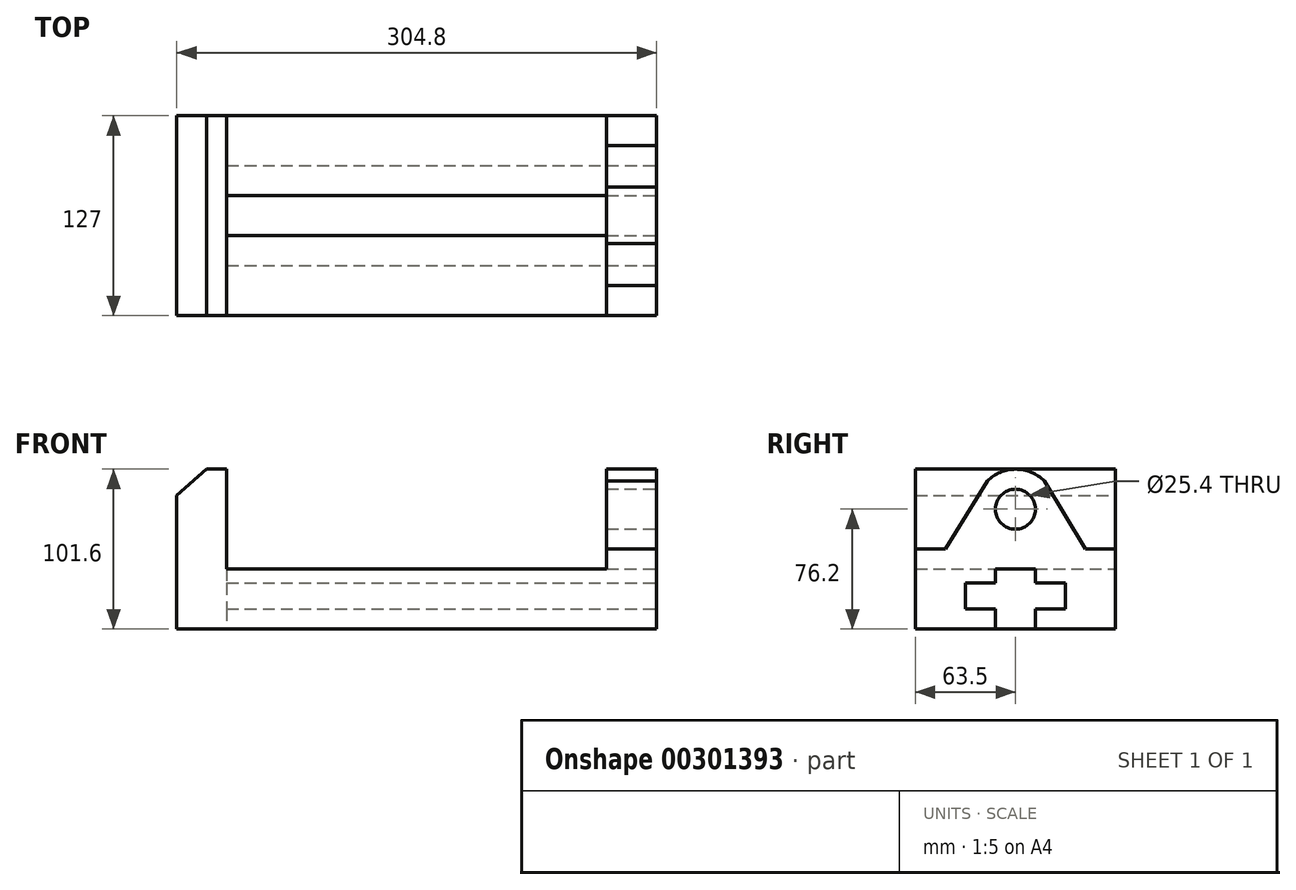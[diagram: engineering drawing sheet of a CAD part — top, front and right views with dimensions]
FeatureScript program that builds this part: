
annotation { "Feature Type Name" : "Feature", "Feature Type Description" : "" }
export const myFeature = defineFeature(function(context is Context, id is Id, definition is map)
    precondition{}
    {
        {
            var Q0;
            Q0=qCreatedBy(makeId("Front.planeOp"),FACE);
            var sketch = newSketch(context, id + "F0", { "sketchPlane" : qUnion([Q0])});
            skLineSegment(sketch, "E0", {"start": v(0, 0) * mm, "end": v(304.8, 0) * mm});
            skLineSegment(sketch, "E1", {"start": v(304.8, 0) * mm, "end": v(304.8, 101.6) * mm});
            skLineSegment(sketch, "E2", {"start": v(304.8, 101.6) * mm, "end": v(273.05, 101.6) * mm});
            skLineSegment(sketch, "E3", {"start": v(273.05, 101.6) * mm, "end": v(273.05, 38.1) * mm});
            skLineSegment(sketch, "E4", {"start": v(273.05, 38.1) * mm, "end": v(31.75, 38.1) * mm});
            skLineSegment(sketch, "E5", {"start": v(31.75, 38.1) * mm, "end": v(31.75, 101.6) * mm});
            skLineSegment(sketch, "E6", {"start": v(31.75, 101.6) * mm, "end": v(19.05, 101.6) * mm});
            skLineSegment(sketch, "E7", {"start": v(0, 84.8) * mm, "end": v(0, 0) * mm});
            skLineSegment(sketch, "E8", {"start": v(0, 84.8) * mm, "end": v(19.05, 101.6) * mm});
            skSolve(sketch);
        }
        {
            var Q0;
            Q0=makeQuery(id+"F0.imprint","IMPRINT",FACE,{"disambiguationData":[TD([[makeQuery(id+"F0.imprint","IMPRINT",EDGE,{"derivedFrom":sQuery(id+"F0.wireOp",EDGE,"E0")}),1.0]])]});
            extrude(context, id + "F1", {"entities" : qUnion([Q0]), "depth" : 127 * mm});
        }
        {
            var Q0;
            Q0=makeQuery(id+"F1.opExtrude","SWEPT_FACE",FACE,{"disambiguationData":[OSD([sQuery(id+"F0.wireOp",EDGE,"E1")])]});
            var sketch = newSketch(context, id + "F2", { "sketchPlane" : qUnion([Q0])});
            skLineSegment(sketch, "E9", {"start": v(-63.5, 101.6) * mm, "end": v(-63.5, 0) * mm, "construction": true});
            skLineSegment(sketch, "E10", {"start": v(-50.8, 0) * mm, "end": v(-50.8, 12.7) * mm});
            skLineSegment(sketch, "E11", {"start": v(-50.8, 12.7) * mm, "end": v(-31.75, 12.7) * mm});
            skLineSegment(sketch, "E12", {"start": v(-31.75, 12.7) * mm, "end": v(-31.75, 29.2) * mm});
            skLineSegment(sketch, "E13", {"start": v(-31.75, 29.2) * mm, "end": v(-50.8, 29.2) * mm});
            skLineSegment(sketch, "E14", {"start": v(-50.8, 29.2) * mm, "end": v(-50.8, 38.1) * mm});
            skLineSegment(sketch, "E15", {"start": v(-50.8, 38.1) * mm, "end": v(-76.2, 38.1) * mm});
            skLineSegment(sketch, "E16", {"start": v(-76.2, 38.1) * mm, "end": v(-76.2, 29.2) * mm});
            skLineSegment(sketch, "E17", {"start": v(-76.2, 29.2) * mm, "end": v(-95.25, 29.2) * mm});
            skLineSegment(sketch, "E18", {"start": v(-95.25, 29.2) * mm, "end": v(-95.25, 12.7) * mm});
            skLineSegment(sketch, "E19", {"start": v(-95.25, 12.7) * mm, "end": v(-76.2, 12.7) * mm});
            skLineSegment(sketch, "E20", {"start": v(-76.2, 12.7) * mm, "end": v(-76.2, 0) * mm});
            skLineSegment(sketch, "E21", {"start": v(-76.2, 0) * mm, "end": v(-50.8, 0) * mm});
            skLineSegment(sketch, "E22", {"start": v(-127, 50.8) * mm, "end": v(-107.95, 50.8) * mm});
            skLineSegment(sketch, "E23", {"start": v(-107.95, 50.8) * mm, "end": v(-81.3, 94.08) * mm});
            skLineSegment(sketch, "E24", {"start": v(-45.23, 94.08) * mm, "end": v(-19.05, 50.8) * mm});
            skLineSegment(sketch, "E25", {"start": v(-19.05, 50.8) * mm, "end": v(0, 50.8) * mm});
            skArc(sketch, "E26", {"start": v(-45.23, 94.08) * mm, "mid": v(-63.27, 101.6) * mm, "end": v(-81.3, 94.08) * mm});
            skCircle(sketch, "E27", {"center": v(-63.5, 76.2) * mm, "radius": 12.7 * mm});
            skLineSegment(sketch, "E28", {"start": v(-127, 76.2) * mm, "end": v(0, 76.2) * mm, "construction": true});
            skSolve(sketch);
        }
        {
            var Q0;
            {var subQ6=sQuery(id+"F2.wireOp",EDGE,"E22");Q0=makeQuery(id+"F2.imprint","IMPRINT",FACE,{"disambiguationData":[TD([[makeQuery(id+"F2.imprint","IMPRINT",EDGE,{"derivedFrom":subQ6}),1.0]])]});}
            var Q1;
            {var subQ6=sQuery(id+"F2.wireOp",EDGE,"E24");Q1=makeQuery(id+"F2.imprint","IMPRINT",FACE,{"disambiguationData":[TD([[makeQuery(id+"F2.imprint","IMPRINT",EDGE,{"derivedFrom":subQ6}),1.0]])]});}
            var Q2;
            Q2=makeQuery(id+"F2.imprint","IMPRINT",FACE,{"disambiguationData":[TD([[makeQuery(id+"F2.imprint","IMPRINT",EDGE,{"derivedFrom":sQuery(id+"F2.wireOp",EDGE,"E10")}),1.0]])]});
            var Q3;
            Q3=makeQuery(id+"F2.imprint","IMPRINT",FACE,{"disambiguationData":[TD([[makeQuery(id+"F2.imprint","IMPRINT",EDGE,{"derivedFrom":sQuery(id+"F2.wireOp",EDGE,"E27")}),1.0]])]});
            extrude(context, id + "F3", {"entities" : qUnion([Q0, Q1, Q2, Q3]), "operationType" : NewBodyOperationType.REMOVE, "oppositeDirection" : true, "depth" : 50.8 * mm});
        }
        {
            var Q0;
            Q0=makeQuery(id+"F3.boolean.opBoolean","COPY",FACE,{"derivedFrom":makeQuery(id+"F3.opExtrude","CAP_FACE",FACE,{"disambiguationData":[OSD([sQuery(id+"F2.wireOp",EDGE,"E10"),sQuery(id+"F2.wireOp",EDGE,"E11"),sQuery(id+"F2.wireOp",EDGE,"E12"),sQuery(id+"F2.wireOp",EDGE,"E13"),sQuery(id+"F2.wireOp",EDGE,"E14"),sQuery(id+"F2.wireOp",EDGE,"E15"),sQuery(id+"F2.wireOp",EDGE,"E16"),sQuery(id+"F2.wireOp",EDGE,"E17"),sQuery(id+"F2.wireOp",EDGE,"E18"),sQuery(id+"F2.wireOp",EDGE,"E19"),sQuery(id+"F2.wireOp",EDGE,"E20"),sQuery(id+"F2.wireOp",EDGE,"E21")])],"isStart":false})});
            extrude(context, id + "F4", {"entities" : qUnion([Q0]), "operationType" : NewBodyOperationType.REMOVE, "oppositeDirection" : true, "depth" : 222.25 * mm});
        }
    });
